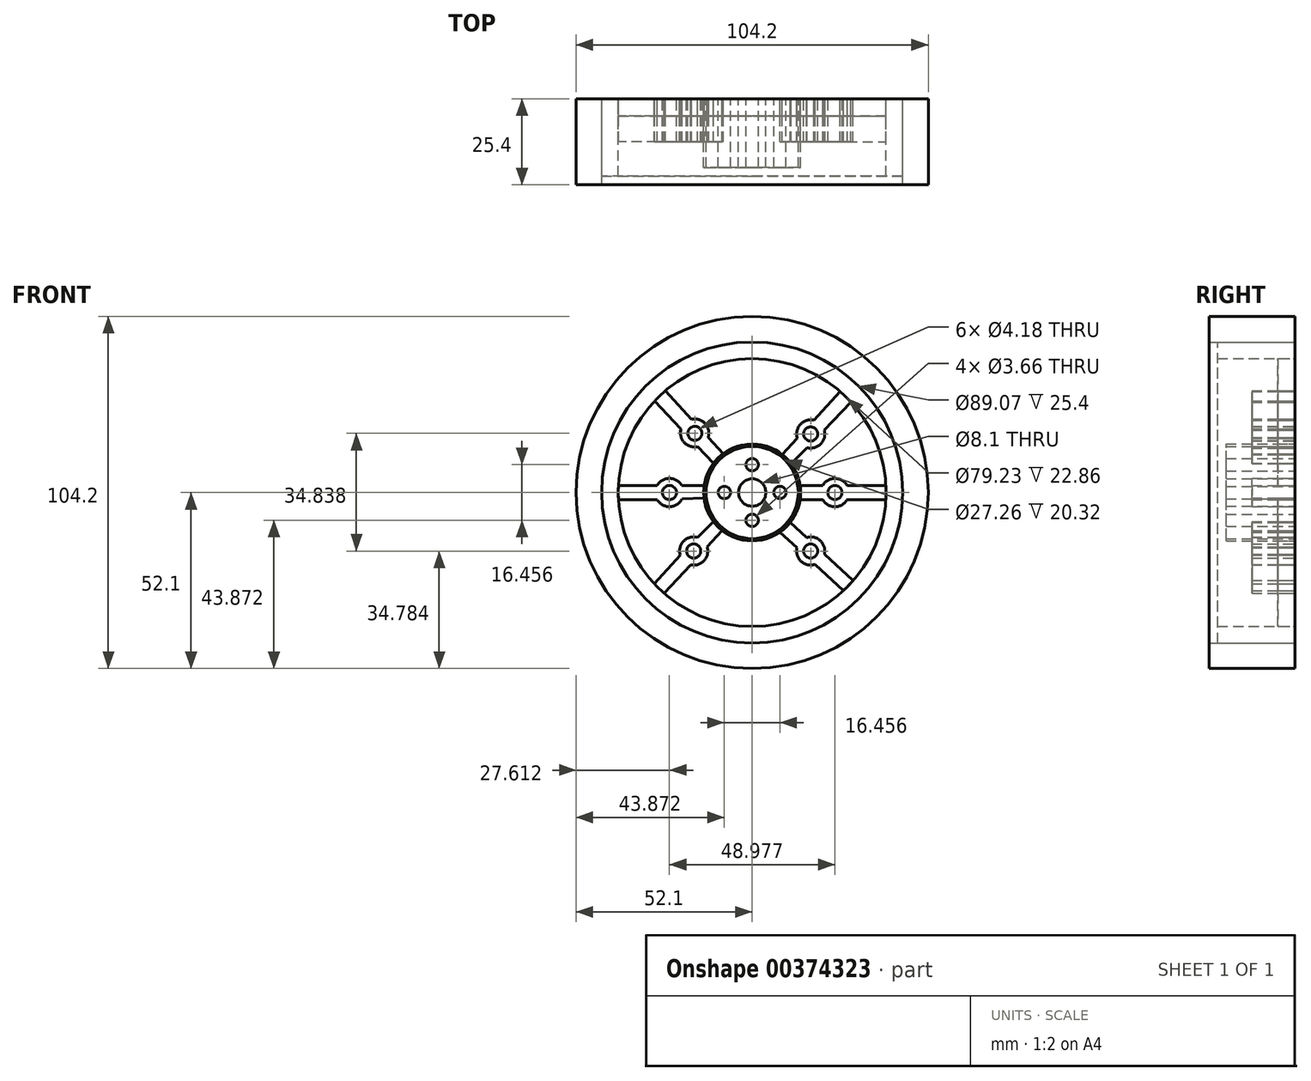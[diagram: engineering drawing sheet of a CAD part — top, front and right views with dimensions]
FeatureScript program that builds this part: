
annotation { "Feature Type Name" : "Feature", "Feature Type Description" : "" }
export const myFeature = defineFeature(function(context is Context, id is Id, definition is map)
    precondition{}
    {
        {
            var Q0;
            Q0=qCreatedBy(makeId("Front.planeOp"),FACE);
            var sketch = newSketch(context, id + "F0", { "sketchPlane" : qUnion([Q0])});
            skCircle(sketch, "E0", {"center": v(0, 0) * mm, "radius": 52.24 * mm});
            skCircle(sketch, "E1", {"center": v(0, 0) * mm, "radius": 4.05 * mm});
            skCircle(sketch, "E2", {"center": v(0, 0) * mm, "radius": 8.23 * mm});
            skCircle(sketch, "E3", {"center": v(0, 0) * mm, "radius": 13.06 * mm});
            skCircle(sketch, "E4", {"center": v(0, -8.23) * mm, "radius": 1.83 * mm});
            skCircle(sketch, "E5", {"center": v(8.23, 0) * mm, "radius": 1.83 * mm});
            skCircle(sketch, "E6", {"center": v(0, 8.23) * mm, "radius": 1.83 * mm});
            skCircle(sketch, "E7", {"center": v(-8.23, 0) * mm, "radius": 1.83 * mm});
            skCircle(sketch, "E8", {"center": v(0, 0) * mm, "radius": 14.34 * mm});
            skCircle(sketch, "E9", {"center": v(0, 0) * mm, "radius": 13.63 * mm});
            skCircle(sketch, "E10", {"center": v(24.49, 0) * mm, "radius": 2.09 * mm});
            skCircle(sketch, "E11", {"center": v(-24.49, 0) * mm, "radius": 2.09 * mm});
            skCircle(sketch, "E12", {"center": v(17.32, 17.32) * mm, "radius": 2.09 * mm});
            skCircle(sketch, "E13", {"center": v(17.32, -17.32) * mm, "radius": 2.09 * mm});
            skCircle(sketch, "E14", {"center": v(-17.32, -17.32) * mm, "radius": 2.09 * mm});
            skLineSegment(sketch, "E15", {"start": v(20.87, 2.09) * mm, "end": v(14.18, 2.09) * mm});
            skLineSegment(sketch, "E16", {"start": v(20.87, -2.09) * mm, "end": v(14.18, -2.09) * mm});
            skArc(sketch, "E17", {"start": v(28.1, 2.09) * mm, "mid": v(24.49, 4.16) * mm, "end": v(20.87, 2.09) * mm});
            skArc(sketch, "E18", {"start": v(20.87, -2.09) * mm, "mid": v(24.49, -4.2) * mm, "end": v(28.1, -2.09) * mm});
            skLineSegment(sketch, "E19", {"start": v(-20.87, 2.09) * mm, "end": v(-14.18, 2.09) * mm});
            skLineSegment(sketch, "E20", {"start": v(-20.78, -1.93) * mm, "end": v(-14.24, -1.65) * mm});
            skArc(sketch, "E21", {"start": v(-20.87, 2.09) * mm, "mid": v(-24.49, 4.19) * mm, "end": v(-28.1, 2.09) * mm});
            skArc(sketch, "E22", {"start": v(-28.1, -2.09) * mm, "mid": v(-24.4, -4.18) * mm, "end": v(-20.78, -1.93) * mm});
            skLineSegment(sketch, "E23", {"start": v(13.33, 16.06) * mm, "end": v(8.9, 11.24) * mm});
            skLineSegment(sketch, "E24", {"start": v(16.25, 13.27) * mm, "end": v(11.54, 8.5) * mm});
            skArc(sketch, "E25", {"start": v(18.22, 21.4) * mm, "mid": v(14.24, 20.14) * mm, "end": v(13.33, 16.06) * mm});
            skArc(sketch, "E26", {"start": v(16.25, 13.27) * mm, "mid": v(20.31, 14.4) * mm, "end": v(21.33, 18.49) * mm});
            skLineSegment(sketch, "E27", {"start": v(-13.33, -16.06) * mm, "end": v(-8.9, -11.24) * mm});
            skLineSegment(sketch, "E28", {"start": v(-16.2, -13.29) * mm, "end": v(-11.46, -8.61) * mm});
            skArc(sketch, "E29", {"start": v(-18.22, -21.4) * mm, "mid": v(-14.23, -20.15) * mm, "end": v(-13.33, -16.06) * mm});
            skArc(sketch, "E30", {"start": v(-16.2, -13.29) * mm, "mid": v(-20.32, -14.42) * mm, "end": v(-21.3, -18.58) * mm});
            skLineSegment(sketch, "E31", {"start": v(16.06, -13.33) * mm, "end": v(11.24, -8.9) * mm});
            skLineSegment(sketch, "E32", {"start": v(13.24, -16.4) * mm, "end": v(8.2, -11.76) * mm});
            skArc(sketch, "E33", {"start": v(21.4, -18.22) * mm, "mid": v(20.13, -14.25) * mm, "end": v(16.06, -13.33) * mm});
            skArc(sketch, "E34", {"start": v(13.24, -16.4) * mm, "mid": v(14.5, -20.38) * mm, "end": v(18.58, -21.3) * mm});
            skCircle(sketch, "E35", {"center": v(0, 0) * mm, "radius": 39.61 * mm});
            skCircle(sketch, "E36", {"center": v(0, 0) * mm, "radius": 44.53 * mm});
            skCircle(sketch, "E37", {"center": v(0, 0) * mm, "radius": 52.1 * mm});
            skLineSegment(sketch, "E38", {"start": v(26.01, 29.88) * mm, "end": v(18.22, 21.4) * mm});
            skLineSegment(sketch, "E39", {"start": v(29.24, 26.73) * mm, "end": v(21.33, 18.49) * mm});
            skLineSegment(sketch, "E40", {"start": v(39.56, 2.09) * mm, "end": v(28.1, 2.09) * mm});
            skLineSegment(sketch, "E41", {"start": v(39.56, -2.09) * mm, "end": v(28.1, -2.09) * mm});
            skLineSegment(sketch, "E42", {"start": v(29.88, -26.01) * mm, "end": v(21.4, -18.22) * mm});
            skLineSegment(sketch, "E43", {"start": v(26.98, -29.01) * mm, "end": v(18.58, -21.3) * mm});
            skLineSegment(sketch, "E44", {"start": v(-29.01, -26.98) * mm, "end": v(-21.3, -18.58) * mm});
            skLineSegment(sketch, "E45", {"start": v(-26.01, -29.88) * mm, "end": v(-18.22, -21.4) * mm});
            skLineSegment(sketch, "E46", {"start": v(-39.56, 2.09) * mm, "end": v(-28.1, 2.09) * mm});
            skLineSegment(sketch, "E47", {"start": v(-39.56, -2.09) * mm, "end": v(-28.1, -2.09) * mm});
            skLineSegment(sketch, "E48.0.1", {"start": v(-8.58, 11.48) * mm, "end": v(-13.01, 16.3) * mm});
            skArc(sketch, "E48.0.2", {"start": v(-13.01, 16.3) * mm, "mid": v(-13.92, 20.4) * mm, "end": v(-17.92, 21.66) * mm});
            skLineSegment(sketch, "E48.0.3", {"start": v(-17.92, 21.66) * mm, "end": v(-25.7, 30.14) * mm});
            skLineSegment(sketch, "E48.0.5", {"start": v(-28.92, 27.07) * mm, "end": v(-21.06, 18.8) * mm});
            skArc(sketch, "E48.0.6", {"start": v(-21.06, 18.8) * mm, "mid": v(-20.08, 14.76) * mm, "end": v(-16.1, 13.57) * mm});
            skLineSegment(sketch, "E48.0.7", {"start": v(-16.1, 13.57) * mm, "end": v(-11.43, 8.65) * mm});
            skCircle(sketch, "E49.0", {"center": v(-16.97, 17.52) * mm, "radius": 2.09 * mm});
            skLineSegment(sketch, "E50", {"start": v(-13.01, 16.3) * mm, "end": v(-8.58, 11.48) * mm});
            skArc(sketch, "E51", {"start": v(-21.06, 18.8) * mm, "mid": v(-20.09, 14.75) * mm, "end": v(-16.1, 13.57) * mm});
            skSolve(sketch);
        }
        {
            var Q0;
            Q0=qCreatedBy(makeId("Front.planeOp"),FACE);
            var sketch = newSketch(context, id + "F1", { "sketchPlane" : qUnion([Q0])});
            skArc(sketch, "E52.0.0", {"start": v(8.9, 11.24) * mm, "mid": v(10.3, 9.96) * mm, "end": v(11.54, 8.5) * mm});
            skLineSegment(sketch, "E52.0.1", {"start": v(11.54, 8.5) * mm, "end": v(16.25, 13.27) * mm});
            skArc(sketch, "E52.0.2", {"start": v(16.25, 13.27) * mm, "mid": v(20.31, 14.4) * mm, "end": v(21.33, 18.49) * mm});
            skLineSegment(sketch, "E52.0.3", {"start": v(21.33, 18.49) * mm, "end": v(29.24, 26.73) * mm});
            skArc(sketch, "E52.0.4", {"start": v(29.24, 26.73) * mm, "mid": v(27.67, 28.35) * mm, "end": v(26.01, 29.88) * mm});
            skLineSegment(sketch, "E52.0.5", {"start": v(26.01, 29.88) * mm, "end": v(18.22, 21.4) * mm});
            skArc(sketch, "E52.0.6", {"start": v(18.22, 21.4) * mm, "mid": v(14.24, 20.14) * mm, "end": v(13.33, 16.06) * mm});
            skLineSegment(sketch, "E52.0.7", {"start": v(13.33, 16.06) * mm, "end": v(8.9, 11.24) * mm});
            skCircle(sketch, "E53.0.0", {"center": v(17.32, 17.32) * mm, "radius": 2.09 * mm});
            skArc(sketch, "E54.0.0", {"start": v(39.56, -2.09) * mm, "mid": v(39.61, 0) * mm, "end": v(39.56, 2.09) * mm});
            skLineSegment(sketch, "E54.0.1", {"start": v(39.56, 2.09) * mm, "end": v(28.1, 2.09) * mm});
            skArc(sketch, "E54.0.2", {"start": v(28.1, 2.09) * mm, "mid": v(24.49, 4.16) * mm, "end": v(20.87, 2.09) * mm});
            skLineSegment(sketch, "E54.0.3", {"start": v(20.87, 2.09) * mm, "end": v(14.18, 2.09) * mm});
            skArc(sketch, "E54.0.4", {"start": v(14.18, 2.09) * mm, "mid": v(14.34, 0) * mm, "end": v(14.18, -2.09) * mm});
            skLineSegment(sketch, "E54.0.5", {"start": v(14.18, -2.09) * mm, "end": v(20.87, -2.09) * mm});
            skArc(sketch, "E54.0.6", {"start": v(20.87, -2.09) * mm, "mid": v(24.49, -4.2) * mm, "end": v(28.1, -2.09) * mm});
            skLineSegment(sketch, "E54.0.7", {"start": v(28.1, -2.09) * mm, "end": v(39.56, -2.09) * mm});
            skCircle(sketch, "E54.1.0", {"center": v(24.49, 0) * mm, "radius": 2.09 * mm});
            skLineSegment(sketch, "E55.0.0", {"start": v(18.58, -21.3) * mm, "end": v(26.98, -29.01) * mm});
            skArc(sketch, "E55.0.1", {"start": v(26.98, -29.01) * mm, "mid": v(28.47, -27.55) * mm, "end": v(29.88, -26.01) * mm});
            skLineSegment(sketch, "E55.0.2", {"start": v(29.88, -26.01) * mm, "end": v(21.4, -18.22) * mm});
            skArc(sketch, "E55.0.3", {"start": v(21.4, -18.22) * mm, "mid": v(20.13, -14.25) * mm, "end": v(16.06, -13.33) * mm});
            skLineSegment(sketch, "E55.0.4", {"start": v(16.06, -13.33) * mm, "end": v(11.24, -8.9) * mm});
            skArc(sketch, "E55.0.5", {"start": v(11.24, -8.9) * mm, "mid": v(9.82, -10.44) * mm, "end": v(8.2, -11.76) * mm});
            skLineSegment(sketch, "E55.0.6", {"start": v(8.2, -11.76) * mm, "end": v(13.24, -16.4) * mm});
            skArc(sketch, "E55.0.7", {"start": v(13.24, -16.4) * mm, "mid": v(14.5, -20.38) * mm, "end": v(18.58, -21.3) * mm});
            skCircle(sketch, "E55.1.0", {"center": v(17.32, -17.32) * mm, "radius": 2.09 * mm});
            skLineSegment(sketch, "E56.0.0", {"start": v(-21.3, -18.58) * mm, "end": v(-29.01, -26.98) * mm});
            skArc(sketch, "E56.0.1", {"start": v(-29.01, -26.98) * mm, "mid": v(-27.55, -28.47) * mm, "end": v(-26.01, -29.88) * mm});
            skLineSegment(sketch, "E56.0.2", {"start": v(-26.01, -29.88) * mm, "end": v(-18.22, -21.4) * mm});
            skArc(sketch, "E56.0.3", {"start": v(-18.22, -21.4) * mm, "mid": v(-14.23, -20.15) * mm, "end": v(-13.33, -16.06) * mm});
            skLineSegment(sketch, "E56.0.4", {"start": v(-13.33, -16.06) * mm, "end": v(-8.9, -11.24) * mm});
            skArc(sketch, "E56.0.5", {"start": v(-8.9, -11.24) * mm, "mid": v(-10.26, -10) * mm, "end": v(-11.46, -8.61) * mm});
            skLineSegment(sketch, "E56.0.6", {"start": v(-11.46, -8.61) * mm, "end": v(-16.2, -13.29) * mm});
            skArc(sketch, "E56.0.7", {"start": v(-16.2, -13.29) * mm, "mid": v(-20.32, -14.42) * mm, "end": v(-21.3, -18.58) * mm});
            skCircle(sketch, "E56.1.0", {"center": v(-17.32, -17.32) * mm, "radius": 2.09 * mm});
            skArc(sketch, "E57.0.0", {"start": v(-39.56, 2.09) * mm, "mid": v(-39.61, 0) * mm, "end": v(-39.56, -2.09) * mm});
            skLineSegment(sketch, "E57.0.1", {"start": v(-39.56, -2.09) * mm, "end": v(-28.1, -2.09) * mm});
            skArc(sketch, "E57.0.2", {"start": v(-28.1, -2.09) * mm, "mid": v(-24.4, -4.18) * mm, "end": v(-20.78, -1.93) * mm});
            skLineSegment(sketch, "E57.0.3", {"start": v(-20.78, -1.93) * mm, "end": v(-14.24, -1.65) * mm});
            skArc(sketch, "E57.0.4", {"start": v(-14.24, -1.65) * mm, "mid": v(-14.33, 0.22) * mm, "end": v(-14.18, 2.09) * mm});
            skLineSegment(sketch, "E57.0.5", {"start": v(-14.18, 2.09) * mm, "end": v(-20.87, 2.09) * mm});
            skArc(sketch, "E57.0.6", {"start": v(-20.87, 2.09) * mm, "mid": v(-24.49, 4.19) * mm, "end": v(-28.1, 2.09) * mm});
            skLineSegment(sketch, "E57.0.7", {"start": v(-28.1, 2.09) * mm, "end": v(-39.56, 2.09) * mm});
            skCircle(sketch, "E57.1.0", {"center": v(-24.49, 0) * mm, "radius": 2.09 * mm});
            skArc(sketch, "E58.0.0", {"start": v(-11.43, 8.65) * mm, "mid": v(-10.1, 10.17) * mm, "end": v(-8.58, 11.48) * mm});
            skLineSegment(sketch, "E58.0.1", {"start": v(-8.58, 11.48) * mm, "end": v(-13.01, 16.3) * mm});
            skArc(sketch, "E58.0.2", {"start": v(-13.01, 16.3) * mm, "mid": v(-13.92, 20.4) * mm, "end": v(-17.92, 21.66) * mm});
            skLineSegment(sketch, "E58.0.3", {"start": v(-17.92, 21.66) * mm, "end": v(-25.7, 30.14) * mm});
            skArc(sketch, "E58.0.4", {"start": v(-25.7, 30.14) * mm, "mid": v(-27.36, 28.65) * mm, "end": v(-28.92, 27.07) * mm});
            skLineSegment(sketch, "E58.0.5", {"start": v(-28.92, 27.07) * mm, "end": v(-21.06, 18.8) * mm});
            skArc(sketch, "E58.0.6", {"start": v(-21.06, 18.8) * mm, "mid": v(-20.08, 14.76) * mm, "end": v(-16.1, 13.57) * mm});
            skLineSegment(sketch, "E58.0.7", {"start": v(-16.1, 13.57) * mm, "end": v(-11.43, 8.65) * mm});
            skCircle(sketch, "E59.0.0", {"center": v(-16.97, 17.52) * mm, "radius": 2.09 * mm});
            skSolve(sketch);
        }
        {
            var Q0;
            Q0=makeQuery(id+"F0.imprint","IMPRINT",FACE,{"disambiguationData":[TD([[makeQuery(id+"F0.imprint","IMPRINT",EDGE,{"derivedFrom":sQuery(id+"F0.wireOp",EDGE,"E9")}),-1.0]])]});
            var sketch = newSketch(context, id + "F2", { "sketchPlane" : qUnion([Q0])});
            skCircle(sketch, "E60.0", {"center": v(0, 0) * mm, "radius": 14.34 * mm});
            skCircle(sketch, "E61.0", {"center": v(-8.23, 0) * mm, "radius": 1.83 * mm});
            skCircle(sketch, "E62.0", {"center": v(0, 8.23) * mm, "radius": 1.83 * mm});
            skCircle(sketch, "E63.0", {"center": v(0, -8.23) * mm, "radius": 1.83 * mm});
            skCircle(sketch, "E64.0", {"center": v(8.23, 0) * mm, "radius": 1.83 * mm});
            skCircle(sketch, "E65.0", {"center": v(0, 0) * mm, "radius": 4.05 * mm});
            skSolve(sketch);
        }
        {
            var Q0;
            Q0=qCreatedBy(makeId("Front.planeOp"),FACE);
            var sketch = newSketch(context, id + "F3", { "sketchPlane" : qUnion([Q0])});
            skLineSegment(sketch, "E66.0.0", {"start": v(-21.06, 18.8) * mm, "end": v(-28.92, 27.07) * mm});
            skArc(sketch, "E66.0.1", {"start": v(-28.92, 27.07) * mm, "mid": v(-36.45, 15.52) * mm, "end": v(-39.56, 2.09) * mm});
            skLineSegment(sketch, "E66.0.2", {"start": v(-39.56, 2.09) * mm, "end": v(-28.1, 2.09) * mm});
            skArc(sketch, "E66.0.3", {"start": v(-28.1, 2.09) * mm, "mid": v(-24.49, 4.19) * mm, "end": v(-20.87, 2.09) * mm});
            skLineSegment(sketch, "E66.0.4", {"start": v(-20.87, 2.09) * mm, "end": v(-14.18, 2.09) * mm});
            skArc(sketch, "E66.0.5", {"start": v(-14.18, 2.09) * mm, "mid": v(-13.22, 5.54) * mm, "end": v(-11.43, 8.65) * mm});
            skLineSegment(sketch, "E66.0.6", {"start": v(-11.43, 8.65) * mm, "end": v(-16.1, 13.57) * mm});
            skArc(sketch, "E66.0.7", {"start": v(-16.1, 13.57) * mm, "mid": v(-20.09, 14.75) * mm, "end": v(-21.06, 18.8) * mm});
            skLineSegment(sketch, "E67.0.0", {"start": v(18.22, 21.4) * mm, "end": v(26.01, 29.88) * mm});
            skArc(sketch, "E67.0.1", {"start": v(26.01, 29.88) * mm, "mid": v(0.2, 39.61) * mm, "end": v(-25.7, 30.14) * mm});
            skLineSegment(sketch, "E67.0.2", {"start": v(-25.7, 30.14) * mm, "end": v(-17.92, 21.66) * mm});
            skArc(sketch, "E67.0.3", {"start": v(-17.92, 21.66) * mm, "mid": v(-13.92, 20.4) * mm, "end": v(-13.01, 16.3) * mm});
            skLineSegment(sketch, "E67.0.4", {"start": v(-13.01, 16.3) * mm, "end": v(-8.58, 11.48) * mm});
            skArc(sketch, "E67.0.5", {"start": v(-8.58, 11.48) * mm, "mid": v(0.2, 14.33) * mm, "end": v(8.9, 11.24) * mm});
            skLineSegment(sketch, "E67.0.6", {"start": v(8.9, 11.24) * mm, "end": v(13.33, 16.06) * mm});
            skArc(sketch, "E67.0.7", {"start": v(13.33, 16.06) * mm, "mid": v(14.24, 20.14) * mm, "end": v(18.22, 21.4) * mm});
            skArc(sketch, "E68.0.0", {"start": v(39.56, 2.09) * mm, "mid": v(36.54, 15.3) * mm, "end": v(29.24, 26.73) * mm});
            skLineSegment(sketch, "E68.0.1", {"start": v(29.24, 26.73) * mm, "end": v(21.33, 18.49) * mm});
            skArc(sketch, "E68.0.2", {"start": v(21.33, 18.49) * mm, "mid": v(20.31, 14.4) * mm, "end": v(16.25, 13.27) * mm});
            skLineSegment(sketch, "E68.0.3", {"start": v(16.25, 13.27) * mm, "end": v(11.54, 8.5) * mm});
            skArc(sketch, "E68.0.4", {"start": v(11.54, 8.5) * mm, "mid": v(13.25, 5.46) * mm, "end": v(14.18, 2.09) * mm});
            skLineSegment(sketch, "E68.0.5", {"start": v(14.18, 2.09) * mm, "end": v(20.87, 2.09) * mm});
            skArc(sketch, "E68.0.6", {"start": v(20.87, 2.09) * mm, "mid": v(24.49, 4.16) * mm, "end": v(28.1, 2.09) * mm});
            skLineSegment(sketch, "E68.0.7", {"start": v(28.1, 2.09) * mm, "end": v(39.56, 2.09) * mm});
            skLineSegment(sketch, "E69.0.0", {"start": v(21.4, -18.22) * mm, "end": v(29.88, -26.01) * mm});
            skArc(sketch, "E69.0.1", {"start": v(29.88, -26.01) * mm, "mid": v(36.72, -14.86) * mm, "end": v(39.56, -2.09) * mm});
            skLineSegment(sketch, "E69.0.2", {"start": v(39.56, -2.09) * mm, "end": v(28.1, -2.09) * mm});
            skArc(sketch, "E69.0.3", {"start": v(28.1, -2.09) * mm, "mid": v(24.49, -4.2) * mm, "end": v(20.87, -2.09) * mm});
            skLineSegment(sketch, "E69.0.4", {"start": v(20.87, -2.09) * mm, "end": v(14.18, -2.09) * mm});
            skArc(sketch, "E69.0.5", {"start": v(14.18, -2.09) * mm, "mid": v(13.16, -5.69) * mm, "end": v(11.24, -8.9) * mm});
            skLineSegment(sketch, "E69.0.6", {"start": v(11.24, -8.9) * mm, "end": v(16.06, -13.33) * mm});
            skArc(sketch, "E69.0.7", {"start": v(16.06, -13.33) * mm, "mid": v(20.13, -14.25) * mm, "end": v(21.4, -18.22) * mm});
            skLineSegment(sketch, "E70.0.0", {"start": v(-18.22, -21.4) * mm, "end": v(-26.01, -29.88) * mm});
            skArc(sketch, "E70.0.1", {"start": v(-26.01, -29.88) * mm, "mid": v(0.65, -39.6) * mm, "end": v(26.98, -29.01) * mm});
            skLineSegment(sketch, "E70.0.2", {"start": v(26.98, -29.01) * mm, "end": v(18.58, -21.3) * mm});
            skArc(sketch, "E70.0.3", {"start": v(18.58, -21.3) * mm, "mid": v(14.5, -20.38) * mm, "end": v(13.24, -16.4) * mm});
            skLineSegment(sketch, "E70.0.4", {"start": v(13.24, -16.4) * mm, "end": v(8.2, -11.76) * mm});
            skArc(sketch, "E70.0.5", {"start": v(8.2, -11.76) * mm, "mid": v(-0.44, -14.33) * mm, "end": v(-8.9, -11.24) * mm});
            skLineSegment(sketch, "E70.0.6", {"start": v(-8.9, -11.24) * mm, "end": v(-13.33, -16.06) * mm});
            skArc(sketch, "E70.0.7", {"start": v(-13.33, -16.06) * mm, "mid": v(-14.23, -20.15) * mm, "end": v(-18.22, -21.4) * mm});
            skLineSegment(sketch, "E71.0.0", {"start": v(-28.1, -2.09) * mm, "end": v(-39.56, -2.09) * mm});
            skArc(sketch, "E71.0.1", {"start": v(-39.56, -2.09) * mm, "mid": v(-36.47, -15.46) * mm, "end": v(-29.01, -26.98) * mm});
            skLineSegment(sketch, "E71.0.2", {"start": v(-29.01, -26.98) * mm, "end": v(-21.3, -18.58) * mm});
            skArc(sketch, "E71.0.3", {"start": v(-21.3, -18.58) * mm, "mid": v(-20.32, -14.42) * mm, "end": v(-16.2, -13.29) * mm});
            skLineSegment(sketch, "E71.0.4", {"start": v(-16.2, -13.29) * mm, "end": v(-11.46, -8.61) * mm});
            skArc(sketch, "E71.0.5", {"start": v(-11.46, -8.61) * mm, "mid": v(-13.31, -5.32) * mm, "end": v(-14.24, -1.65) * mm});
            skLineSegment(sketch, "E71.0.6", {"start": v(-14.24, -1.65) * mm, "end": v(-20.78, -1.93) * mm});
            skArc(sketch, "E71.0.7", {"start": v(-20.78, -1.93) * mm, "mid": v(-24.4, -4.18) * mm, "end": v(-28.1, -2.09) * mm});
            skSolve(sketch);
        }
        {
            var Q0;
            Q0=makeQuery(id+"F0.imprint","IMPRINT",FACE,{"disambiguationData":[TD([[makeQuery(id+"F0.imprint","IMPRINT",EDGE,{"derivedFrom":sQuery(id+"F0.wireOp",EDGE,"E36")}),-1.0]])]});
            extrude(context, id + "F4", {"entities" : qUnion([Q0]), "depth" : 25.4 * mm});
        }
        {
            var Q0;
            Q0=qSketchRegion(id+"F1",true);
            extrude(context, id + "F5", {"entities" : qUnion([Q0]), "depth" : 12.7 * mm});
        }
        {
            var Q0;
            Q0=makeQuery(id+"F2.imprint","IMPRINT",FACE,{"disambiguationData":[TD([[makeQuery(id+"F2.imprint","IMPRINT",EDGE,{"derivedFrom":sQuery(id+"F2.wireOp",EDGE,"E61.0")}),-1.0]])]});
            var Q1;
            Q1=makeQuery(id+"F0.imprint","IMPRINT",FACE,{"disambiguationData":[TD([[makeQuery(id+"F0.imprint","IMPRINT",EDGE,{"derivedFrom":sQuery(id+"F0.wireOp",EDGE,"E9")}),-1.0]])]});
            extrude(context, id + "F6", {"entities" : qUnion([Q0, Q1]), "depth" : 20.32 * mm});
        }
        {
            var Q0;
            Q0=qSketchRegion(id+"F3",true);
            extrude(context, id + "F7", {"entities" : qUnion([Q0]), "depth" : 5.08 * mm});
        }
        {
            var Q0;
            Q0=makeQuery(id+"F0.imprint","IMPRINT",FACE,{"disambiguationData":[TD([[makeQuery(id+"F0.imprint","IMPRINT",EDGE,{"derivedFrom":sQuery(id+"F0.wireOp",EDGE,"E36")}),1.0]])]});
            var sketch = newSketch(context, id + "F8", { "sketchPlane" : qUnion([Q0])});
            skCircle(sketch, "E72.0.0", {"center": v(0, 0) * mm, "radius": 44.53 * mm});
            skSolve(sketch);
        }
        {
            var Q0;
            Q0=makeQuery(id+"F8.imprint","IMPRINT",FACE,{"disambiguationData":[TD([[makeQuery(id+"F8.imprint","IMPRINT",EDGE,{"derivedFrom":sQuery(id+"F8.wireOp",EDGE,"E72.0.0")}),1.0]])]});
            extrude(context, id + "F9", {"entities" : qUnion([Q0]), "depth" : 22.86 * mm});
        }
    });
